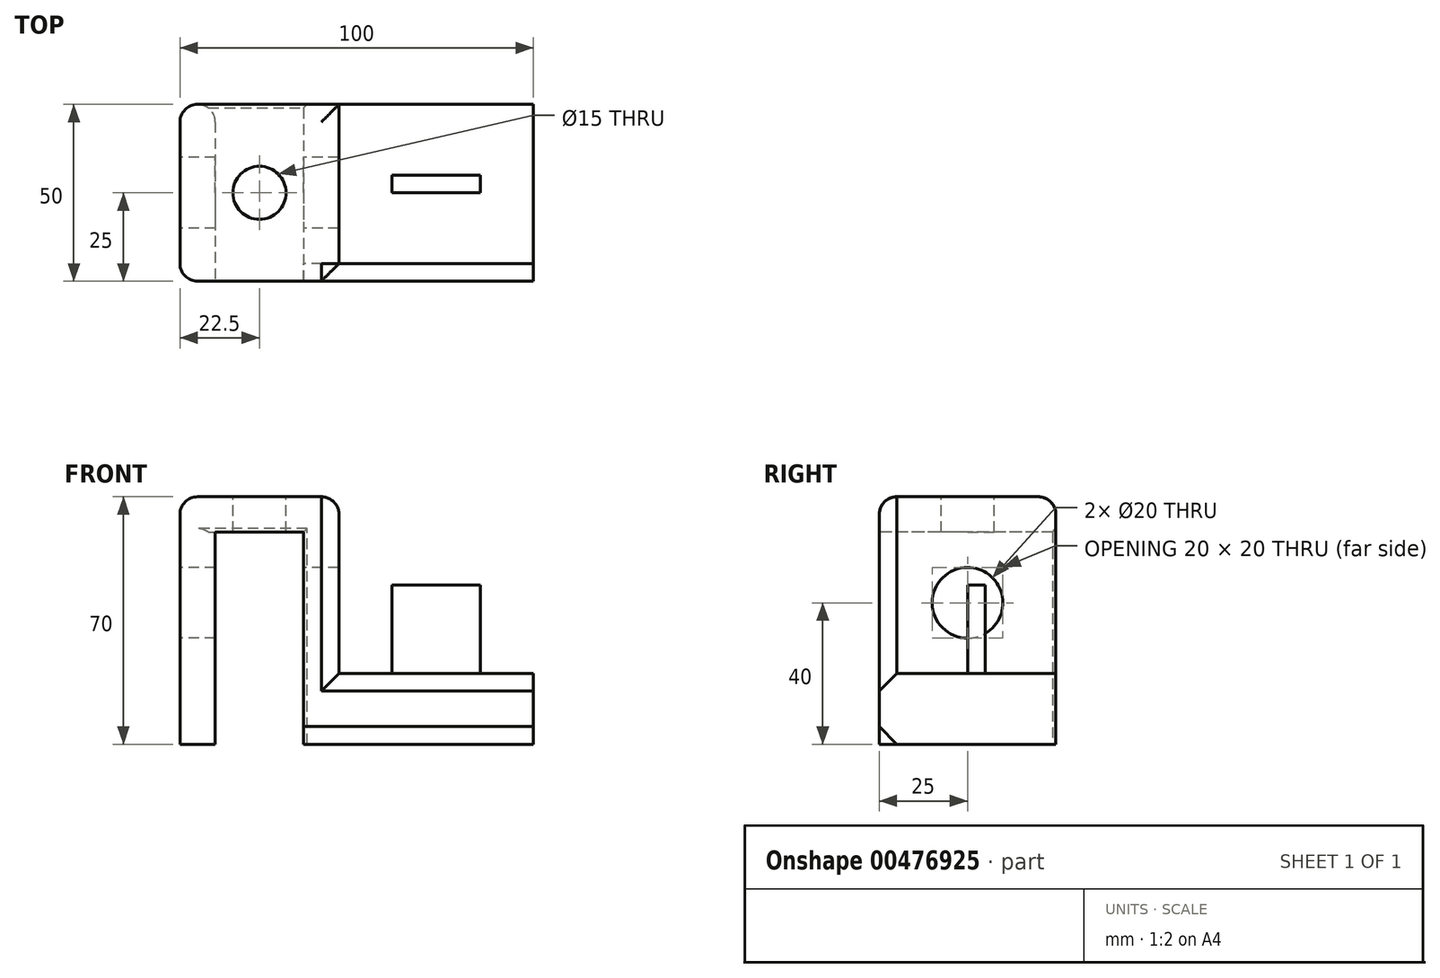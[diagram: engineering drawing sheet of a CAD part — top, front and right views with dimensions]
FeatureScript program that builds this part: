
annotation { "Feature Type Name" : "Feature", "Feature Type Description" : "" }
export const myFeature = defineFeature(function(context is Context, id is Id, definition is map)
    precondition{}
    {
        {
            var Q0;
            Q0=qCreatedBy(makeId("Top.planeOp"),FACE);
            var sketch = newSketch(context, id + "F0", { "sketchPlane" : qUnion([Q0])});
            skLineSegment(sketch, "E0.bottom", {"start": v(0, 0) * mm, "end": v(100, 0) * mm});
            skLineSegment(sketch, "E0.top", {"start": v(0, 50) * mm, "end": v(100, 50) * mm});
            skLineSegment(sketch, "E0.left", {"start": v(0, 0) * mm, "end": v(0, 50) * mm});
            skLineSegment(sketch, "E0.right", {"start": v(100, 0) * mm, "end": v(100, 50) * mm});
            skSolve(sketch);
        }
        {
            var Q0;
            Q0 = qSketchRegion(id + "F0", true);
            extrude(context, id + "F1", {"entities" : qUnion([Q0]), "depth" : 20 * mm});
        }
        {
            var Q0;
            Q0=makeQuery(id+"F1.opExtrude","CAP_FACE",FACE,{"disambiguationData":[OSD([sQuery(id+"F0.wireOp",EDGE,"E0.bottom"),sQuery(id+"F0.wireOp",EDGE,"E0.top"),sQuery(id+"F0.wireOp",EDGE,"E0.left"),sQuery(id+"F0.wireOp",EDGE,"E0.right")])],"isStart":false});
            var sketch = newSketch(context, id + "F2", { "sketchPlane" : qUnion([Q0])});
            skLineSegment(sketch, "E1.bottom", {"start": v(0, 0) * mm, "end": v(45, 0) * mm});
            skLineSegment(sketch, "E1.top", {"start": v(0, 50) * mm, "end": v(45, 50) * mm});
            skLineSegment(sketch, "E1.left", {"start": v(0, 0) * mm, "end": v(0, 50) * mm});
            skLineSegment(sketch, "E1.right", {"start": v(45, 0) * mm, "end": v(45, 50) * mm});
            skSolve(sketch);
        }
        {
            var Q0;
            Q0 = qSketchRegion(id + "F2", true);
            extrude(context, id + "F3", {"entities" : qUnion([Q0]), "operationType" : NewBodyOperationType.ADD, "depth" : 50 * mm});
        }
        {
            var Q0;
            Q0=makeQuery(id+"F3.boolean.opBoolean","MERGE",FACE,{"derivedFrom":[makeQuery(id+"F1.opExtrude","SWEPT_FACE",FACE,{"disambiguationData":[OSD([sQuery(id+"F0.wireOp",EDGE,"E0.bottom")])]}),makeQuery(id+"F3.opExtrude","SWEPT_FACE",FACE,{"disambiguationData":[OSD([sQuery(id+"F2.wireOp",EDGE,"E1.bottom")])]})]});
            var sketch = newSketch(context, id + "F4", { "sketchPlane" : qUnion([Q0])});
            skLineSegment(sketch, "E2.bottom", {"start": v(10, 0) * mm, "end": v(35, 0) * mm});
            skLineSegment(sketch, "E2.top", {"start": v(10, 60) * mm, "end": v(35, 60) * mm});
            skLineSegment(sketch, "E2.left", {"start": v(10, 0) * mm, "end": v(10, 60) * mm});
            skLineSegment(sketch, "E2.right", {"start": v(35, 0) * mm, "end": v(35, 60) * mm});
            skSolve(sketch);
        }
        {
            var Q0;
            Q0 = qSketchRegion(id + "F4", true);
            extrude(context, id + "F5", {"entities" : qUnion([Q0]), "operationType" : NewBodyOperationType.REMOVE, "endBound" : BoundingType.THROUGH_ALL, "oppositeDirection" : true, "depth" : 25 * mm});
        }
        {
            var Q0;
            Q0=makeQuery(id+"F3.boolean.opBoolean","MERGE",FACE,{"derivedFrom":[makeQuery(id+"F1.opExtrude","SWEPT_FACE",FACE,{"disambiguationData":[OSD([sQuery(id+"F0.wireOp",EDGE,"E0.left")])]}),makeQuery(id+"F3.opExtrude","SWEPT_FACE",FACE,{"disambiguationData":[OSD([sQuery(id+"F2.wireOp",EDGE,"E1.left")])]})]});
            var sketch = newSketch(context, id + "F6", { "sketchPlane" : qUnion([Q0])});
            skCircle(sketch, "E3", {"center": v(-25, 40) * mm, "radius": 10 * mm});
            skSolve(sketch);
        }
        {
            var Q0;
            Q0 = qSketchRegion(id + "F6", true);
            var Q1;
            Q1=makeQuery(id+"F3.opExtrude","SWEPT_FACE",FACE,{"disambiguationData":[OSD([sQuery(id+"F2.wireOp",EDGE,"E1.right")])]});
            extrude(context, id + "F7", {"entities" : qUnion([Q0]), "operationType" : NewBodyOperationType.REMOVE, "endBound" : BoundingType.UP_TO_SURFACE, "oppositeDirection" : true, "endBoundEntityFace" : qUnion([Q1]), "depth" : 25 * mm});
        }
        {
            var Q0;
            Q0=makeQuery(id+"F3.opExtrude","CAP_FACE",FACE,{"disambiguationData":[OSD([sQuery(id+"F2.wireOp",EDGE,"E1.bottom"),sQuery(id+"F2.wireOp",EDGE,"E1.top"),sQuery(id+"F2.wireOp",EDGE,"E1.left"),sQuery(id+"F2.wireOp",EDGE,"E1.right")])],"isStart":false});
            var sketch = newSketch(context, id + "F8", { "sketchPlane" : qUnion([Q0])});
            skLineSegment(sketch, "E4", {"start": v(45, 50) * mm, "end": v(0, 0) * mm, "construction": true});
            skLineSegment(sketch, "E5", {"start": v(0, 50) * mm, "end": v(45, 0) * mm, "construction": true});
            skCircle(sketch, "E6", {"center": v(22.5, 25) * mm, "radius": 7.5 * mm});
            skSolve(sketch);
        }
        {
            var Q0;
            Q0 = qSketchRegion(id + "F8", true);
            extrude(context, id + "F9", {"entities" : qUnion([Q0]), "operationType" : NewBodyOperationType.REMOVE, "endBound" : BoundingType.UP_TO_NEXT, "oppositeDirection" : true, "depth" : 25 * mm});
        }
        {
            var Q0;
            Q0=makeQuery(id+"F5.boolean.opBoolean","INTERSECT",EDGE,{"derivedFrom":[makeQuery(id+"F3.boolean.opBoolean","MERGE",FACE,{"derivedFrom":[makeQuery(id+"F1.opExtrude","SWEPT_FACE",FACE,{"disambiguationData":[OSD([sQuery(id+"F0.wireOp",EDGE,"E0.top")])]}),makeQuery(id+"F3.opExtrude","SWEPT_FACE",FACE,{"disambiguationData":[OSD([sQuery(id+"F2.wireOp",EDGE,"E1.top")])]})]}),makeQuery(id+"F5.opExtrude","SWEPT_FACE",FACE,{"disambiguationData":[OSD([sQuery(id+"F4.wireOp",EDGE,"E2.top")])]})]});
            var Q1;
            Q1=makeQuery(id+"F5.boolean.opBoolean","INTERSECT",EDGE,{"derivedFrom":[makeQuery(id+"F3.boolean.opBoolean","MERGE",FACE,{"derivedFrom":[makeQuery(id+"F1.opExtrude","SWEPT_FACE",FACE,{"disambiguationData":[OSD([sQuery(id+"F0.wireOp",EDGE,"E0.top")])]}),makeQuery(id+"F3.opExtrude","SWEPT_FACE",FACE,{"disambiguationData":[OSD([sQuery(id+"F2.wireOp",EDGE,"E1.top")])]})]}),makeQuery(id+"F5.opExtrude","SWEPT_FACE",FACE,{"disambiguationData":[OSD([sQuery(id+"F4.wireOp",EDGE,"E2.right")])]})]});
            chamfer(context, id + "F10", {"entities" : qUnion([Q0, Q1]), "width" : 1 * mm, "tangentPropagation" : true});
        }
        {
            var Q0;
            Q0=makeQuery(id+"F3.opExtrude","CAP_EDGE",EDGE,{"disambiguationData":[OSD([sQuery(id+"F2.wireOp",EDGE,"E1.top")])],"isStart":false});
            var Q1;
            Q1=makeQuery(id+"F3.opExtrude","CAP_EDGE",EDGE,{"disambiguationData":[OSD([sQuery(id+"F2.wireOp",EDGE,"E1.left")])],"isStart":false});
            var Q2;
            Q2=makeQuery(id+"F3.opExtrude","CAP_EDGE",EDGE,{"disambiguationData":[OSD([sQuery(id+"F2.wireOp",EDGE,"E1.bottom")])],"isStart":false});
            var Q3;
            Q3=makeQuery(id+"F3.opExtrude","CAP_EDGE",EDGE,{"disambiguationData":[OSD([sQuery(id+"F2.wireOp",EDGE,"E1.right")])],"isStart":false});
            var Q4;
            Q4=makeQuery(id+"F3.boolean.opBoolean","MERGE",EDGE,{"derivedFrom":[makeQuery(id+"F1.opExtrude","SWEPT_EDGE",EDGE,{"disambiguationData":[OSD([sQuery(id+"F0.wireOp",EDGE,"E0.top"),sQuery(id+"F0.wireOp",EDGE,"E0.left")])]}),makeQuery(id+"F3.opExtrude","SWEPT_EDGE",EDGE,{"disambiguationData":[OSD([sQuery(id+"F2.wireOp",EDGE,"E1.top"),sQuery(id+"F2.wireOp",EDGE,"E1.left")])]})]});
            var Q5;
            Q5=makeQuery(id+"F5.boolean.opBoolean","INTERSECT",EDGE,{"derivedFrom":[makeQuery(id+"F3.boolean.opBoolean","MERGE",FACE,{"derivedFrom":[makeQuery(id+"F1.opExtrude","SWEPT_FACE",FACE,{"disambiguationData":[OSD([sQuery(id+"F0.wireOp",EDGE,"E0.top")])]}),makeQuery(id+"F3.opExtrude","SWEPT_FACE",FACE,{"disambiguationData":[OSD([sQuery(id+"F2.wireOp",EDGE,"E1.top")])]})]}),makeQuery(id+"F5.opExtrude","SWEPT_FACE",FACE,{"disambiguationData":[OSD([sQuery(id+"F4.wireOp",EDGE,"E2.left")])]})]});
            var Q6;
            Q6=makeQuery(id+"F3.boolean.opBoolean","MERGE",EDGE,{"derivedFrom":[makeQuery(id+"F1.opExtrude","SWEPT_EDGE",EDGE,{"disambiguationData":[OSD([sQuery(id+"F0.wireOp",EDGE,"E0.bottom"),sQuery(id+"F0.wireOp",EDGE,"E0.left")])]}),makeQuery(id+"F3.opExtrude","SWEPT_EDGE",EDGE,{"disambiguationData":[OSD([sQuery(id+"F2.wireOp",EDGE,"E1.bottom"),sQuery(id+"F2.wireOp",EDGE,"E1.left")])]})]});
            var Q7;
            Q7=makeQuery(id+"F5.boolean.opBoolean","COPY",EDGE,{"derivedFrom":makeQuery(id+"F5.opExtrude","CAP_EDGE",EDGE,{"disambiguationData":[OSD([sQuery(id+"F4.wireOp",EDGE,"E2.left")])],"isStart":true})});
            fillet(context, id + "F11", {"entities" : qUnion([Q0, Q1, Q2, Q3, Q4, Q5, Q6, Q7]), "radius" : 5 * mm, "tangentPropagation" : true, "allowEdgeOverflow" : false});
        }
        {
            var Q0;
            Q0=makeQuery(id+"F5.boolean.opBoolean","COPY",EDGE,{"derivedFrom":makeQuery(id+"F5.opExtrude","CAP_EDGE",EDGE,{"disambiguationData":[OSD([sQuery(id+"F4.wireOp",EDGE,"E2.right")])],"isStart":true})});
            var Q1;
            {var subQ0=sQuery(id+"F0.wireOp",EDGE,"E0.right");var subQ1=sQuery(id+"F0.wireOp",EDGE,"E0.bottom");Q1=makeQuery(id+"F5.boolean.opBoolean","SPLIT",EDGE,{"disambiguationData":[TD([makeQuery(id+"F1.opExtrude","SWEPT_FACE",FACE,{"disambiguationData":[OSD([subQ0])]})])],"derivedFrom":makeQuery(id+"F1.opExtrude","CAP_EDGE",EDGE,{"disambiguationData":[OSD([subQ1])],"isStart":true})});}
            var Q2;
            Q2=makeQuery(id+"F1.opExtrude","CAP_EDGE",EDGE,{"disambiguationData":[OSD([sQuery(id+"F0.wireOp",EDGE,"E0.bottom")])],"isStart":false});
            var Q3;
            Q3=makeQuery(id+"F3.opExtrude","SWEPT_EDGE",EDGE,{"disambiguationData":[OSD([sQuery(id+"F0.wireOp",EDGE,"E0.bottom"),sQuery(id+"F2.wireOp",EDGE,"E1.bottom"),sQuery(id+"F2.wireOp",EDGE,"E1.right")])]});
            chamfer(context, id + "F12", {"entities" : qUnion([Q0, Q1, Q2, Q3]), "width" : 5 * mm, "tangentPropagation" : true});
        }
        {
            var Q0;
            Q0=makeQuery(id+"F1.opExtrude","CAP_FACE",FACE,{"disambiguationData":[OSD([sQuery(id+"F0.wireOp",EDGE,"E0.bottom"),sQuery(id+"F0.wireOp",EDGE,"E0.top"),sQuery(id+"F0.wireOp",EDGE,"E0.left"),sQuery(id+"F0.wireOp",EDGE,"E0.right")])],"isStart":false});
            var sketch = newSketch(context, id + "F13", { "sketchPlane" : qUnion([Q0])});
            skLineSegment(sketch, "E7.bottom", {"start": v(60, 25) * mm, "end": v(85, 25) * mm});
            skLineSegment(sketch, "E7.top", {"start": v(60, 30) * mm, "end": v(85, 30) * mm});
            skLineSegment(sketch, "E7.left", {"start": v(60, 25) * mm, "end": v(60, 30) * mm});
            skLineSegment(sketch, "E7.right", {"start": v(85, 25) * mm, "end": v(85, 30) * mm});
            skSolve(sketch);
        }
        {
            var Q0;
            Q0 = qSketchRegion(id + "F13", true);
            extrude(context, id + "F14", {"entities" : qUnion([Q0]), "operationType" : NewBodyOperationType.ADD, "depth" : 25 * mm});
        }
    });
